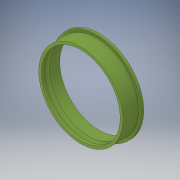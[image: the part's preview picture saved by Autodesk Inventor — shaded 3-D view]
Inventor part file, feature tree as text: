
AUTODESK INVENTOR PART (.ipt)
format: ipt  version: 2018 (Build 220112000, 112)  size: 150,016 bytes
history: native  units: in
note: dims shown in document units (in); Inventor stores cm internally (conversion verified against a paired STEP export)
features: sketch x3, extrude x2, revolve x1, projected_geometry x1
ambient origin geometry x8: Origin, YZ Plane, XZ Plane, XY Plane, X Axis, Y Axis, Z Axis, Center Point
bodies: Solid1 (feature_tree)
feature tree (7):
  revolve  "Revolution1"  [1 undecoded]
  sketch  "Sketch2"  dims[d3=0.25in d4=0.25in]
  extrude  "Extrusion1"  Depth=0.25in
  extrude  "Extrusion2"  Depth=0.135in
  sketch  "Sketch1"  dims[d1=1.875in d2=0.124in]
  projected_geometry  "Projected Loop1"
  sketch  "Sketch3"  dims[d5=0.0675in d6=0.135in d7=90.0deg d8=0.125in d9=0.25in d10=0.0in d11=0.125in d12=0.0in]
note: 1 required parameter value undecoded (feature->parameter linkage not recoverable at this tier; creation-order binding heuristic only, values carry confidence <= 0.55)
